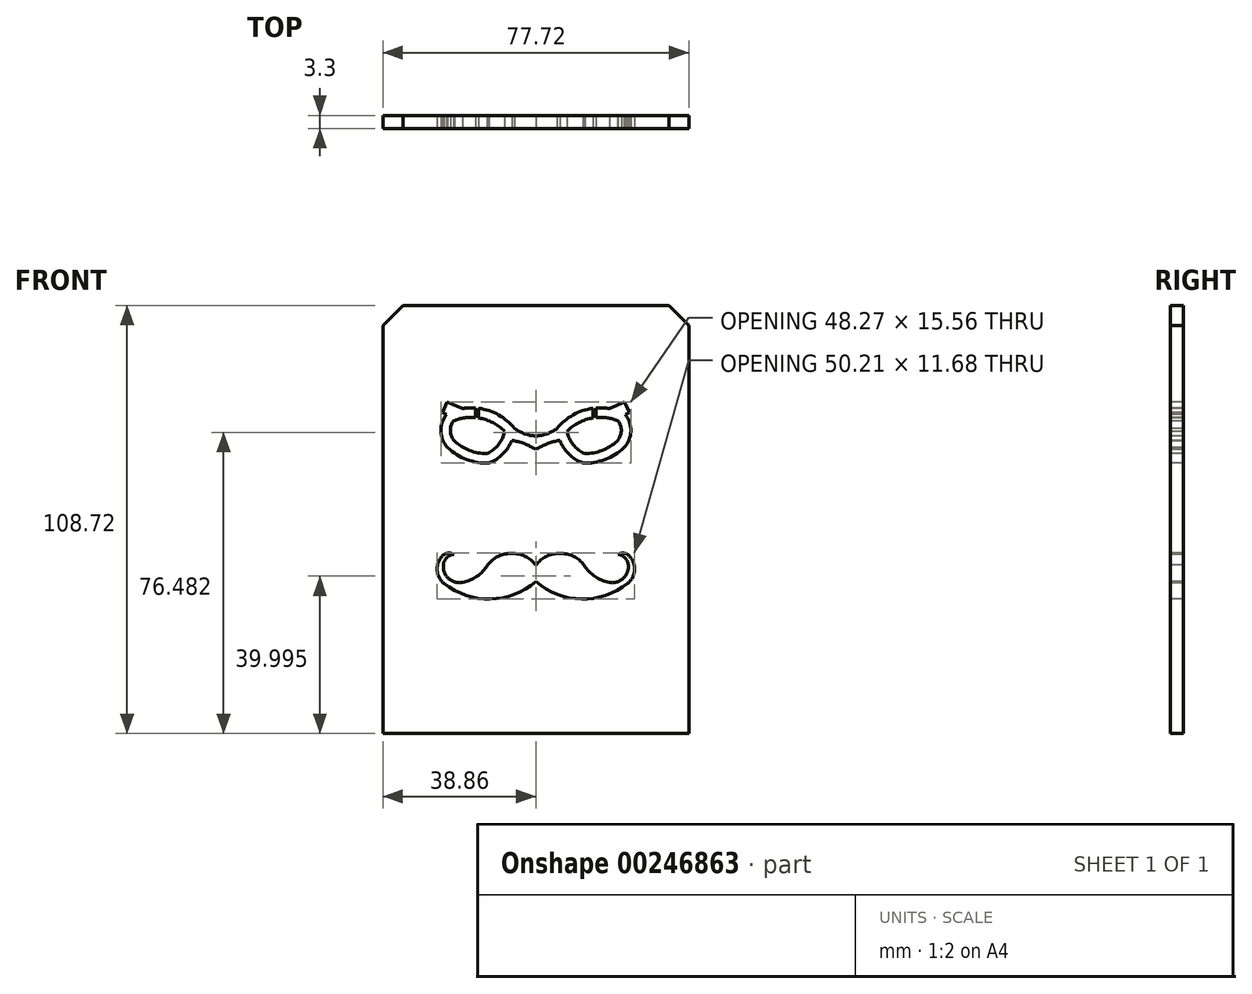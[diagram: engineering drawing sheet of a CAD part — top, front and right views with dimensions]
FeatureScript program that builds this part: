
annotation { "Feature Type Name" : "Feature", "Feature Type Description" : "" }
export const myFeature = defineFeature(function(context is Context, id is Id, definition is map)
    precondition{}
    {
        {
            var Q0;
            Q0=qCreatedBy(makeId("Front.planeOp"),FACE);
            var sketch = newSketch(context, id + "F0", { "sketchPlane" : qUnion([Q0])});
            skLineSegment(sketch, "E0.bottom", {"start": v(38.86, 54.36) * mm, "end": v(-38.86, 54.36) * mm});
            skLineSegment(sketch, "E0.top", {"start": v(38.86, -54.36) * mm, "end": v(-38.86, -54.36) * mm});
            skLineSegment(sketch, "E0.left", {"start": v(38.86, 54.36) * mm, "end": v(38.86, -54.36) * mm});
            skLineSegment(sketch, "E0.right", {"start": v(-38.86, 54.36) * mm, "end": v(-38.86, -54.36) * mm});
            skPoint(sketch, "E0.middle", {"position": v(0, 0) * mm});
            skSolve(sketch);
        }
        {
            var Q0;
            Q0=qSketchRegion(id+"F0",true);
            extrude(context, id + "F1", {"entities" : qUnion([Q0]), "depth" : 3.3 * mm});
        }
        {
            var Q0;
            Q0=makeQuery(id+"F1.opExtrude","CAP_FACE",FACE,{"disambiguationData":[OSD([sQuery(id+"F0.wireOp",EDGE,"E0.bottom"),sQuery(id+"F0.wireOp",EDGE,"E0.top"),sQuery(id+"F0.wireOp",EDGE,"E0.left"),sQuery(id+"F0.wireOp",EDGE,"E0.right")])],"isStart":false});
            var sketch = newSketch(context, id + "F2", { "sketchPlane" : qUnion([Q0])});
            skLineSegment(sketch, "E1", {"start": v(0, 57.24) * mm, "end": v(0, -57.24) * mm, "construction": true});
            skLineSegment(sketch, "E2", {"start": v(-50.8, 0) * mm, "end": v(50.8, 0) * mm, "construction": true});
            skArc(sketch, "E3", {"start": v(35.44, -3.57) * mm, "mid": v(31.46, -11.87) * mm, "end": v(32.26, -21.03) * mm});
            skLineSegment(sketch, "E4", {"start": v(15.88, -44.54) * mm, "end": v(0, -44.54) * mm, "construction": true});
            skArc(sketch, "E5", {"start": v(15.88, -44.54) * mm, "mid": v(30.2, -37.06) * mm, "end": v(32.26, -21.03) * mm});
            skArc(sketch, "E6", {"start": v(15.88, -44.54) * mm, "mid": v(7.78, -45.34) * mm, "end": v(0, -47.71) * mm});
            skArc(sketch, "E7.MirrorCS", {"start": v(-15.87, -44.54) * mm, "mid": v(-7.78, -45.34) * mm, "end": v(0, -47.71) * mm});
            skArc(sketch, "E8.MirrorCS", {"start": v(-15.87, -44.54) * mm, "mid": v(-30.2, -37.06) * mm, "end": v(-32.26, -21.03) * mm});
            skArc(sketch, "E9.MirrorCS", {"start": v(-35.44, -3.57) * mm, "mid": v(-31.46, -11.87) * mm, "end": v(-32.26, -21.03) * mm});
            skArc(sketch, "E10.MirrorCS", {"start": v(-35.44, 3.57) * mm, "mid": v(-31.46, 11.87) * mm, "end": v(-32.26, 21.03) * mm});
            skArc(sketch, "E11.MirrorCS", {"start": v(-15.88, 44.54) * mm, "mid": v(-30.2, 37.06) * mm, "end": v(-32.26, 21.03) * mm});
            skArc(sketch, "E12.MirrorCS", {"start": v(-15.88, 44.54) * mm, "mid": v(-7.78, 45.34) * mm, "end": v(0, 47.71) * mm});
            skArc(sketch, "E13.MirrorCS", {"start": v(15.87, 44.54) * mm, "mid": v(7.78, 45.34) * mm, "end": v(0, 47.71) * mm});
            skArc(sketch, "E14.MirrorCS", {"start": v(15.87, 44.54) * mm, "mid": v(30.2, 37.06) * mm, "end": v(32.26, 21.03) * mm});
            skArc(sketch, "E15.MirrorCS", {"start": v(35.44, 3.57) * mm, "mid": v(31.46, 11.87) * mm, "end": v(32.26, 21.03) * mm});
            skArc(sketch, "E16", {"start": v(35.44, 3.57) * mm, "mid": v(34.41, 0) * mm, "end": v(35.44, -3.57) * mm});
            skPoint(sketch, "E17.orphan", {"position": v(39.69, 0) * mm});
            skArc(sketch, "E18.MirrorCS", {"start": v(-35.44, 3.57) * mm, "mid": v(-34.41, 0) * mm, "end": v(-35.44, -3.57) * mm});
            skPoint(sketch, "E19.orphan", {"position": v(-39.69, 0) * mm});
            skSolve(sketch);
        }
        {
            var Q0;
            Q0=makeQuery(id+"F2.imprint","IMPRINT",FACE,{"disambiguationData":[TD([[makeQuery(id+"F2.imprint","IMPRINT",EDGE,{"derivedFrom":sQuery(id+"F2.wireOp",EDGE,"E3")}),1.0]])]});
            var sketch = newSketch(context, id + "F3", { "sketchPlane" : qUnion([Q0])});
            skFitSpline(sketch, "E20", {"points": [v(-34.74, -25) * mm, v(-17.68, -23.14) * mm, v(0, -25.84) * mm, v(18.3, -28) * mm, v(33.6, -24.4) * mm], "startDerivative": vector(68.08, 28.42) * mm, "endDerivative": vector(41.75, 55.86) * mm});
            skArc(sketch, "E21.0", {"start": v(15.88, -44.54) * mm, "mid": v(28.97, -38.63) * mm, "end": v(33.2, -24.9) * mm});
            skArc(sketch, "E22.0", {"start": v(-15.87, -44.54) * mm, "mid": v(-29.14, -38.43) * mm, "end": v(-33.13, -24.38) * mm});
            skArc(sketch, "E23.0", {"start": v(15.88, -44.54) * mm, "mid": v(7.78, -45.34) * mm, "end": v(0, -47.71) * mm});
            skArc(sketch, "E23.1", {"start": v(-15.87, -44.54) * mm, "mid": v(-7.78, -45.34) * mm, "end": v(0, -47.71) * mm});
            skPoint(sketch, "E24.orphan", {"position": v(-32.26, -21.03) * mm});
            skLineSegment(sketch, "E25.bottom", {"start": v(23.58, -32.65) * mm, "end": v(5.44, -32.65) * mm, "construction": true});
            skLineSegment(sketch, "E25.top", {"start": v(23.58, -12.55) * mm, "end": v(5.44, -12.55) * mm, "construction": true});
            skLineSegment(sketch, "E25.left", {"start": v(23.58, -32.65) * mm, "end": v(23.58, -12.55) * mm, "construction": true});
            skLineSegment(sketch, "E25.right", {"start": v(5.44, -32.65) * mm, "end": v(5.44, -12.55) * mm, "construction": true});
            skArc(sketch, "E26", {"start": v(6.5, -26.77) * mm, "mid": v(6.6, -19.6) * mm, "end": v(5.44, -12.55) * mm});
            skArc(sketch, "E27", {"start": v(23.58, -12.55) * mm, "mid": v(22.47, -20.37) * mm, "end": v(22.78, -28.26) * mm});
            skLineSegment(sketch, "E28", {"start": v(0.57, -13.45) * mm, "end": v(5.44, -12.55) * mm});
            skLineSegment(sketch, "E29", {"start": v(28.46, 0) * mm, "end": v(0.57, 0) * mm, "construction": true});
            skArc(sketch, "E30", {"start": v(-2.4, -8.48) * mm, "mid": v(-2.65, -12) * mm, "end": v(0.57, -13.45) * mm});
            skArc(sketch, "E31", {"start": v(0, -10.42) * mm, "mid": v(-0.23, -8.24) * mm, "end": v(-2.4, -8.48) * mm});
            skArc(sketch, "E32", {"start": v(0, -10.42) * mm, "mid": v(-0.04, -11.92) * mm, "end": v(1.4, -12.35) * mm});
            skArc(sketch, "E33", {"start": v(1.4, -12.35) * mm, "mid": v(5.55, -5.86) * mm, "end": v(0.57, 0) * mm});
            skLineSegment(sketch, "E34", {"start": v(14.51, 0) * mm, "end": v(14.51, -12.55) * mm, "construction": true});
            skArc(sketch, "E35.MirrorCS", {"start": v(27.61, -12.35) * mm, "mid": v(23.47, -5.86) * mm, "end": v(28.46, 0) * mm});
            skLineSegment(sketch, "E36.MirrorCS", {"start": v(28.46, -13.45) * mm, "end": v(23.58, -12.55) * mm});
            skArc(sketch, "E37.MirrorCS", {"start": v(31.42, -8.48) * mm, "mid": v(31.67, -12) * mm, "end": v(28.46, -13.45) * mm});
            skArc(sketch, "E38.MirrorCS", {"start": v(29.02, -10.42) * mm, "mid": v(29.25, -8.24) * mm, "end": v(31.42, -8.48) * mm});
            skArc(sketch, "E39.MirrorCS", {"start": v(29.02, -10.42) * mm, "mid": v(29.06, -11.92) * mm, "end": v(27.61, -12.35) * mm});
            skArc(sketch, "E40", {"start": v(0.57, 0) * mm, "mid": v(5.65, -0.6) * mm, "end": v(10.76, -0.93) * mm});
            skLineSegment(sketch, "E41", {"start": v(10.76, -0.93) * mm, "end": v(8.47, 9.06) * mm});
            skLineSegment(sketch, "E42", {"start": v(8.47, 9.06) * mm, "end": v(6.8, 8.68) * mm});
            skArc(sketch, "E43", {"start": v(7.7, 9.94) * mm, "mid": v(5.6, 10.49) * mm, "end": v(6.8, 8.68) * mm});
            skLineSegment(sketch, "E44", {"start": v(14.51, 0) * mm, "end": v(14.77, 8.31) * mm, "construction": true});
            skLineSegment(sketch, "E45.MirrorCS", {"start": v(18.26, -0.93) * mm, "end": v(21.1, 8.66) * mm});
            skLineSegment(sketch, "E46.MirrorCS", {"start": v(21.1, 8.66) * mm, "end": v(22.75, 8.18) * mm});
            skArc(sketch, "E47.MirrorCS", {"start": v(21.93, 9.5) * mm, "mid": v(24.07, 9.9) * mm, "end": v(22.75, 8.18) * mm});
            skArc(sketch, "E48", {"start": v(7.7, 9.94) * mm, "mid": v(12.62, 15.22) * mm, "end": v(14.1, 22.28) * mm});
            skArc(sketch, "E49", {"start": v(15.59, 22.28) * mm, "mid": v(17.1, 15.06) * mm, "end": v(21.93, 9.5) * mm});
            skLineSegment(sketch, "E50", {"start": v(14.1, 22.28) * mm, "end": v(12.75, 29.94) * mm});
            skLineSegment(sketch, "E51", {"start": v(12.75, 29.94) * mm, "end": v(10.25, 29.5) * mm});
            skLineSegment(sketch, "E52", {"start": v(10.25, 29.5) * mm, "end": v(10.04, 30.72) * mm});
            skLineSegment(sketch, "E53", {"start": v(10.04, 30.72) * mm, "end": v(12.66, 31.3) * mm});
            skLineSegment(sketch, "E54", {"start": v(12.66, 31.3) * mm, "end": v(12.12, 34.79) * mm});
            skLineSegment(sketch, "E55", {"start": v(12.12, 34.79) * mm, "end": v(14.24, 35.11) * mm});
            skLineSegment(sketch, "E56", {"start": v(14.24, 35.11) * mm, "end": v(14.8, 31.45) * mm});
            skLineSegment(sketch, "E57", {"start": v(14.8, 31.45) * mm, "end": v(17.72, 31.9) * mm});
            skLineSegment(sketch, "E58", {"start": v(17.72, 31.9) * mm, "end": v(17.99, 30.17) * mm});
            skLineSegment(sketch, "E59", {"start": v(17.99, 30.17) * mm, "end": v(14.89, 29.68) * mm});
            skLineSegment(sketch, "E60", {"start": v(14.89, 29.68) * mm, "end": v(15.59, 22.28) * mm});
            skArc(sketch, "E61.trimOffspring", {"start": v(18.26, -0.93) * mm, "mid": v(23.37, -0.6) * mm, "end": v(28.46, 0) * mm});
            skPoint(sketch, "E62.orphan", {"position": v(18.2, -1.17) * mm});
            skLineSegment(sketch, "E63", {"start": v(8.48, -4.98) * mm, "end": v(9.12, -7.41) * mm});
            skLineSegment(sketch, "E64", {"start": v(9.77, -9.85) * mm, "end": v(10.94, -9.54) * mm});
            skLineSegment(sketch, "E65", {"start": v(12.72, -9.06) * mm, "end": v(12.26, -7.34) * mm});
            skLineSegment(sketch, "E66", {"start": v(11.56, -4.7) * mm, "end": v(10.33, -4.82) * mm});
            skLineSegment(sketch, "E67", {"start": v(9.75, -4.87) * mm, "end": v(10.34, -7.13) * mm});
            skLineSegment(sketch, "E68", {"start": v(10.34, -7.13) * mm, "end": v(9.12, -7.41) * mm});
            skLineSegment(sketch, "E69", {"start": v(10.33, -4.82) * mm, "end": v(10.9, -7.06) * mm});
            skLineSegment(sketch, "E70", {"start": v(10.9, -7.06) * mm, "end": v(12.14, -6.89) * mm});
            skLineSegment(sketch, "E71", {"start": v(9.29, -8.05) * mm, "end": v(10.46, -7.73) * mm});
            skLineSegment(sketch, "E72", {"start": v(10.46, -7.73) * mm, "end": v(10.94, -9.54) * mm});
            skLineSegment(sketch, "E73", {"start": v(11.57, -9.37) * mm, "end": v(11.12, -7.64) * mm});
            skLineSegment(sketch, "E74", {"start": v(11.12, -7.64) * mm, "end": v(12.26, -7.34) * mm});
            skLineSegment(sketch, "E75.trimOffspring", {"start": v(12.14, -6.89) * mm, "end": v(11.56, -4.7) * mm});
            skLineSegment(sketch, "E76.trimOffspring", {"start": v(9.75, -4.87) * mm, "end": v(8.48, -4.98) * mm});
            skLineSegment(sketch, "E77.trimOffspring", {"start": v(9.29, -8.05) * mm, "end": v(9.77, -9.85) * mm});
            skLineSegment(sketch, "E78.trimOffspring", {"start": v(11.57, -9.37) * mm, "end": v(12.72, -9.06) * mm});
            skLineSegment(sketch, "E79.MirrorCS", {"start": v(17.46, -4.7) * mm, "end": v(18.69, -4.82) * mm});
            skLineSegment(sketch, "E80.MirrorCS", {"start": v(19.27, -4.87) * mm, "end": v(18.68, -7.13) * mm});
            skLineSegment(sketch, "E81.MirrorCS", {"start": v(17.45, -9.37) * mm, "end": v(17.9, -7.64) * mm});
            skLineSegment(sketch, "E82.MirrorCS", {"start": v(18.68, -7.13) * mm, "end": v(19.9, -7.41) * mm});
            skLineSegment(sketch, "E83.MirrorCS", {"start": v(17.9, -7.64) * mm, "end": v(16.76, -7.34) * mm});
            skLineSegment(sketch, "E84.MirrorCS", {"start": v(18.69, -4.82) * mm, "end": v(18.12, -7.06) * mm});
            skLineSegment(sketch, "E85.MirrorCS", {"start": v(16.88, -6.89) * mm, "end": v(17.46, -4.7) * mm});
            skLineSegment(sketch, "E86.MirrorCS", {"start": v(18.12, -7.06) * mm, "end": v(16.88, -6.89) * mm});
            skLineSegment(sketch, "E87.MirrorCS", {"start": v(19.27, -4.87) * mm, "end": v(20.54, -4.98) * mm});
            skLineSegment(sketch, "E88.MirrorCS", {"start": v(20.54, -4.98) * mm, "end": v(19.9, -7.41) * mm});
            skLineSegment(sketch, "E89.MirrorCS", {"start": v(19.73, -8.05) * mm, "end": v(18.56, -7.73) * mm});
            skLineSegment(sketch, "E90.MirrorCS", {"start": v(19.73, -8.05) * mm, "end": v(19.25, -9.85) * mm});
            skLineSegment(sketch, "E91.MirrorCS", {"start": v(19.25, -9.85) * mm, "end": v(18.08, -9.54) * mm});
            skLineSegment(sketch, "E92.MirrorCS", {"start": v(18.56, -7.73) * mm, "end": v(18.08, -9.54) * mm});
            skLineSegment(sketch, "E93.MirrorCS", {"start": v(17.45, -9.37) * mm, "end": v(16.3, -9.06) * mm});
            skLineSegment(sketch, "E94.MirrorCS", {"start": v(16.3, -9.06) * mm, "end": v(16.76, -7.34) * mm});
            skArc(sketch, "E95", {"start": v(14.28, 11.97) * mm, "mid": v(12.23, 10.98) * mm, "end": v(11.15, 8.98) * mm});
            skLineSegment(sketch, "E96", {"start": v(14.28, 11.97) * mm, "end": v(14.28, 8.98) * mm});
            skLineSegment(sketch, "E97", {"start": v(15.17, 4.65) * mm, "end": v(15.17, 7.88) * mm});
            skLineSegment(sketch, "E98", {"start": v(18.4, 8.98) * mm, "end": v(15.17, 8.98) * mm});
            skLineSegment(sketch, "E99", {"start": v(11.1, 7.88) * mm, "end": v(14.28, 7.88) * mm});
            skLineSegment(sketch, "E100.trimOffspring", {"start": v(15.17, 8.98) * mm, "end": v(15.17, 11.98) * mm});
            skLineSegment(sketch, "E101.trimOffspring", {"start": v(15.17, 7.88) * mm, "end": v(18.43, 7.88) * mm});
            skLineSegment(sketch, "E102.trimOffspring", {"start": v(14.28, 7.88) * mm, "end": v(14.28, 4.66) * mm});
            skLineSegment(sketch, "E103.trimOffspring", {"start": v(14.28, 8.98) * mm, "end": v(11.15, 8.98) * mm});
            skArc(sketch, "E104.trimOffspring", {"start": v(11.1, 7.88) * mm, "mid": v(12.14, 5.73) * mm, "end": v(14.28, 4.66) * mm});
            skArc(sketch, "E105.trimOffspring", {"start": v(18.4, 8.98) * mm, "mid": v(17.28, 11.01) * mm, "end": v(15.17, 11.98) * mm});
            skArc(sketch, "E106.trimOffspring", {"start": v(15.17, 4.65) * mm, "mid": v(17.37, 5.7) * mm, "end": v(18.43, 7.88) * mm});
            skLineSegment(sketch, "E107.left", {"start": v(12.04, -27.4) * mm, "end": v(12.04, -21.48) * mm});
            skLineSegment(sketch, "E107.right", {"start": v(16, -27.8) * mm, "end": v(16, -21.48) * mm});
            skArc(sketch, "E108", {"start": v(16, -21.48) * mm, "mid": v(14.02, -19.5) * mm, "end": v(12.04, -21.48) * mm});
            skLineSegment(sketch, "E109", {"start": v(12.04, -27.4) * mm, "end": v(16, -27.8) * mm});
            skArc(sketch, "E110.0", {"start": v(-35.44, -3.57) * mm, "mid": v(-31.46, -11.87) * mm, "end": v(-32.26, -21.03) * mm, "construction": true});
            skArc(sketch, "E110.1", {"start": v(15.87, 44.54) * mm, "mid": v(7.78, 45.34) * mm, "end": v(0, 47.71) * mm});
            skArc(sketch, "E110.2", {"start": v(-15.88, 44.54) * mm, "mid": v(-30.2, 37.06) * mm, "end": v(-32.26, 21.03) * mm, "construction": true});
            skArc(sketch, "E110.3", {"start": v(-35.44, 3.57) * mm, "mid": v(-34.41, 0) * mm, "end": v(-35.44, -3.57) * mm, "construction": true});
            skArc(sketch, "E110.4", {"start": v(-35.44, 3.57) * mm, "mid": v(-31.46, 11.87) * mm, "end": v(-32.26, 21.03) * mm});
            skArc(sketch, "E110.5", {"start": v(-15.88, 44.54) * mm, "mid": v(-7.78, 45.34) * mm, "end": v(0, 47.71) * mm});
            skArc(sketch, "E111", {"start": v(-17.1, 9.66) * mm, "mid": v(-3.37, 14.89) * mm, "end": v(1.5, 28.74) * mm});
            skArc(sketch, "E112", {"start": v(-17.1, 9.66) * mm, "mid": v(-26.87, 8.42) * mm, "end": v(-35.44, 3.57) * mm});
            skArc(sketch, "E113", {"start": v(15.87, 44.54) * mm, "mid": v(5.2, 39.82) * mm, "end": v(1.5, 28.74) * mm});
            skArc(sketch, "E114.trimOffspring", {"start": v(-15.88, 44.54) * mm, "mid": v(-30.2, 37.06) * mm, "end": v(-32.26, 21.03) * mm});
            skArc(sketch, "E115", {"start": v(-24.92, -22.89) * mm, "mid": v(-23.55, -16.2) * mm, "end": v(-24.4, -9.44) * mm});
            skFitSpline(sketch, "E116", {"points": [v(-24.4, -9.44) * mm, v(-26.98, -10.38) * mm, v(-27.97, -8.39) * mm, v(-29.93, -8.52) * mm, v(-30.92, -6) * mm, v(-32.1, -5.52) * mm, v(-32.53, -4.18) * mm, v(-32.18, -3.27) * mm, v(-31.84, -4.44) * mm, v(-31.05, -4.83) * mm, v(-31.49, -2) * mm, v(-30.88, -2.14) * mm, v(-30.1, -5.05) * mm, v(-29.45, -3.57) * mm, v(-28.71, -3.66) * mm, v(-29.54, -5.78) * mm, v(-29.23, -7.17) * mm, v(-27.54, -7.04) * mm, v(-26.28, -8.52) * mm, v(-24.4, -7.6) * mm], "startDerivative": vector(-46.53, -30.94) * mm, "endDerivative": vector(36.03, 29.74) * mm});
            skArc(sketch, "E117", {"start": v(-24.4, -7.6) * mm, "mid": v(-24.93, -4.98) * mm, "end": v(-25.9, -2.49) * mm});
            skFitSpline(sketch, "E118", {"points": [v(-25.9, -2.49) * mm, v(-27.5, -1.49) * mm, v(-28.76, -1.49) * mm, v(-29.23, 0) * mm, v(-31.14, 0) * mm, v(-30.8, 3.42) * mm, v(-29.97, 3.55) * mm, v(-30.27, 1.77) * mm, v(-29.54, 1.72) * mm, v(-28.8, 4.59) * mm, v(-27.67, 4.37) * mm, v(-28.28, 1.98) * mm, v(-27.84, 0) * mm, v(-27.2, 2.46) * mm, v(-25.9, 2.37) * mm, v(-25.9, 0) * mm, v(-24.11, -2.49) * mm, v(-22.72, -5.26) * mm, v(-21.68, -4.18) * mm, v(-23.16, 1.33) * mm, v(-20.82, 1.46) * mm, v(-20.82, 3.02) * mm], "startDerivative": vector(-33.14, 31.82) * mm, "endDerivative": vector(-15.18, 49.9) * mm});
            skFitSpline(sketch, "E119", {"points": [v(-20.82, 3.02) * mm, v(-19.2, 3.92) * mm, v(-20.04, 5.84) * mm, v(-20.82, 8.3) * mm, v(-20.04, 8.38) * mm, v(-19.62, 6.46) * mm, v(-18.62, 5.34) * mm, v(-18.96, 7.3) * mm, v(-18.2, 7.55) * mm, v(-18.12, 4.13) * mm, v(-19.33, 2.25) * mm, v(-19.46, 0.87) * mm, v(-20.82, 0) * mm, v(-20.04, -3.35) * mm, v(-16.32, 0) * mm, v(-17.1, 1.46) * mm, v(-15.74, 3.02) * mm, v(-15.45, 5.84) * mm, v(-14.49, 5.55) * mm, v(-14.82, 3.02) * mm, v(-14.53, 1.46) * mm, v(-13.36, 4) * mm, v(-12.02, 3.02) * mm, v(-14.2, 0) * mm, v(-17.1, -4.06) * mm, v(-17.1, -7.4) * mm, v(-14.36, -5.44) * mm, v(-14.57, -4.1) * mm, v(-12.78, -3.22) * mm, v(-12.53, -1.68) * mm, v(-10.44, -0.8) * mm, v(-10.27, 1.46) * mm, v(-9.35, 0) * mm, v(-8.6, 3.02) * mm, v(-8.1, 0) * mm, v(-9.44, -1.26) * mm, v(-11.31, -3.26) * mm, v(-13.15, -4.6) * mm, v(-13.36, -6.6) * mm, v(-15.78, -8.94) * mm], "startDerivative": vector(94.65, 30.69) * mm, "endDerivative": vector(-102.82, -69.25) * mm});
            skArc(sketch, "E120", {"start": v(-15.78, -8.94) * mm, "mid": v(-16.8, -16.14) * mm, "end": v(-15.78, -23.34) * mm});
            skFitSpline(sketch, "E121", {"points": [v(-22.4, -11.55) * mm, v(-21.43, -13.07) * mm, v(-21.4, -14.11) * mm, v(-20.72, -14.36) * mm, v(-20.54, -13.59) * mm, v(-20.94, -12.02) * mm, v(-21.71, -11.06) * mm, v(-22.67, -10.07) * mm, v(-22.4, -11.55) * mm]});
            skFitSpline(sketch, "E122", {"points": [v(-18.38, -10.1) * mm, v(-19.09, -11.5) * mm, v(-19.21, -12.7) * mm, v(-19.15, -14.02) * mm, v(-18.84, -14.6) * mm, v(-18.38, -14.05) * mm, v(-18.26, -13.1) * mm, v(-18.56, -12.32) * mm, v(-18.29, -11.28) * mm, v(-17.6, -10.38) * mm, v(-18.38, -10.1) * mm]});
            skFitSpline(sketch, "E123", {"points": [v(-20.3, -15.78) * mm, v(-20.35, -17.1) * mm, v(-20.9, -18.47) * mm, v(-21.8, -19.67) * mm, v(-21.9, -21.46) * mm, v(-20.45, -21.43) * mm, v(-19.64, -20.38) * mm, v(-19.43, -18.84) * mm, v(-19.7, -17.85) * mm, v(-19.7, -16.37) * mm, v(-19.43, -15.38) * mm, v(-20.3, -15.78) * mm]});
            skCircle(sketch, "E124", {"center": v(-15.88, 27.08) * mm, "radius": 13.34 * mm});
            skSolve(sketch);
        }
        {
            var Q0;
            Q0=qSketchRegion(id+"F3",true);
            extrude(context, id + "F4", {"entities" : qUnion([Q0]), "operationType" : NewBodyOperationType.ADD, "oppositeDirection" : true, "depth" : 3.3 * mm});
        }
        {
            var Q0;
            Q0=makeQuery(id+"F1.opExtrude","SWEPT_EDGE",EDGE,{"disambiguationData":[OSD([sQuery(id+"F0.wireOp",EDGE,"E0.bottom"),sQuery(id+"F0.wireOp",EDGE,"E0.right")])]});
            var Q1;
            Q1=makeQuery(id+"F1.opExtrude","SWEPT_EDGE",EDGE,{"disambiguationData":[OSD([sQuery(id+"F0.wireOp",EDGE,"E0.bottom"),sQuery(id+"F0.wireOp",EDGE,"E0.left")])]});
            chamfer(context, id + "F5", {"entities" : qUnion([Q0, Q1]), "width" : 5.08 * mm, "tangentPropagation" : true});
        }
        {
            var Q0;
            Q0=makeQuery(id+"F2.imprint","IMPRINT",FACE,{"disambiguationData":[TD([[makeQuery(id+"F2.imprint","IMPRINT",EDGE,{"derivedFrom":sQuery(id+"F2.wireOp",EDGE,"E3")}),-1.0]])]});
            var sketch = newSketch(context, id + "F6", { "sketchPlane" : qUnion([Q0])});
            skArc(sketch, "E125", {"start": v(6.08, 20.1) * mm, "mid": v(8.4, 16.62) * mm, "end": v(11.92, 14.34) * mm});
            skArc(sketch, "E126", {"start": v(11.92, 14.34) * mm, "mid": v(17.55, 15.25) * mm, "end": v(22.4, 18.27) * mm});
            skArc(sketch, "E127", {"start": v(22.4, 18.27) * mm, "mid": v(24.13, 22.42) * mm, "end": v(22.71, 26.69) * mm});
            skArc(sketch, "E128", {"start": v(18.65, 28.2) * mm, "mid": v(16.98, 28.36) * mm, "end": v(15.3, 28.33) * mm});
            skArc(sketch, "E129.0", {"start": v(20.92, 25.07) * mm, "mid": v(18.16, 25.83) * mm, "end": v(15.3, 25.9) * mm});
            skArc(sketch, "E129.1", {"start": v(20.68, 19.97) * mm, "mid": v(21.72, 22.48) * mm, "end": v(20.92, 25.07) * mm});
            skArc(sketch, "E129.2", {"start": v(12.43, 16.74) * mm, "mid": v(16.86, 17.57) * mm, "end": v(20.68, 19.97) * mm});
            skArc(sketch, "E129.3", {"start": v(7.92, 22.36) * mm, "mid": v(9.5, 19) * mm, "end": v(12.43, 16.74) * mm});
            skArc(sketch, "E130", {"start": v(0, 21.24) * mm, "mid": v(2.83, 21.78) * mm, "end": v(5.38, 23.13) * mm});
            skArc(sketch, "E131", {"start": v(6.08, 20.1) * mm, "mid": v(2.93, 19.26) * mm, "end": v(0, 17.8) * mm});
            skLineSegment(sketch, "E132", {"start": v(18.65, 28.2) * mm, "end": v(22.54, 29.9) * mm});
            skLineSegment(sketch, "E133", {"start": v(22.54, 29.9) * mm, "end": v(23.75, 27.14) * mm});
            skLineSegment(sketch, "E134", {"start": v(23.75, 27.14) * mm, "end": v(22.71, 26.69) * mm});
            skPoint(sketch, "E135.orphan", {"position": v(22.4, 27.06) * mm});
            skArc(sketch, "E136", {"start": v(0, -15.75) * mm, "mid": v(11.58, -20.2) * mm, "end": v(23.33, -16.24) * mm});
            skArc(sketch, "E137", {"start": v(23.33, -16.24) * mm, "mid": v(25.1, -12.56) * mm, "end": v(23.33, -8.89) * mm});
            skArc(sketch, "E138", {"start": v(23.33, -8.89) * mm, "mid": v(22.07, -8.52) * mm, "end": v(20.8, -8.89) * mm});
            skArc(sketch, "E139", {"start": v(23.33, -10.83) * mm, "mid": v(22.38, -9.45) * mm, "end": v(20.8, -8.89) * mm});
            skArc(sketch, "E140", {"start": v(18.65, -15.99) * mm, "mid": v(22.45, -14.73) * mm, "end": v(23.33, -10.83) * mm});
            skArc(sketch, "E141", {"start": v(12.27, -11.6) * mm, "mid": v(15, -14.45) * mm, "end": v(18.65, -15.99) * mm});
            skArc(sketch, "E142", {"start": v(12.27, -11.6) * mm, "mid": v(6.14, -8.58) * mm, "end": v(0, -11.6) * mm});
            skArc(sketch, "E143.MirrorCS", {"start": v(-12.27, -11.6) * mm, "mid": v(-6.14, -8.58) * mm, "end": v(0, -11.6) * mm});
            skArc(sketch, "E144.MirrorCS", {"start": v(-12.27, -11.6) * mm, "mid": v(-15, -14.45) * mm, "end": v(-18.65, -15.99) * mm});
            skArc(sketch, "E145.MirrorCS", {"start": v(0, -15.75) * mm, "mid": v(-11.58, -20.2) * mm, "end": v(-23.33, -16.24) * mm});
            skArc(sketch, "E146.MirrorCS", {"start": v(-23.33, -16.24) * mm, "mid": v(-25.1, -12.56) * mm, "end": v(-23.33, -8.89) * mm});
            skArc(sketch, "E147.MirrorCS", {"start": v(-23.33, -8.89) * mm, "mid": v(-22.07, -8.52) * mm, "end": v(-20.8, -8.89) * mm});
            skArc(sketch, "E148.MirrorCS", {"start": v(-23.33, -10.83) * mm, "mid": v(-22.38, -9.45) * mm, "end": v(-20.8, -8.89) * mm});
            skArc(sketch, "E149.MirrorCS", {"start": v(-18.65, -15.99) * mm, "mid": v(-22.45, -14.73) * mm, "end": v(-23.33, -10.83) * mm});
            skArc(sketch, "E150.MirrorCS", {"start": v(0, 21.24) * mm, "mid": v(-2.83, 21.78) * mm, "end": v(-5.38, 23.13) * mm});
            skArc(sketch, "E151.MirrorCS", {"start": v(-6.08, 20.1) * mm, "mid": v(-2.93, 19.26) * mm, "end": v(0, 17.8) * mm});
            skArc(sketch, "E152.MirrorCS", {"start": v(-6.08, 20.1) * mm, "mid": v(-8.4, 16.62) * mm, "end": v(-11.92, 14.34) * mm});
            skArc(sketch, "E153.MirrorCS", {"start": v(-11.92, 14.34) * mm, "mid": v(-17.55, 15.25) * mm, "end": v(-22.4, 18.27) * mm});
            skArc(sketch, "E154.MirrorCS", {"start": v(-12.43, 16.74) * mm, "mid": v(-16.86, 17.57) * mm, "end": v(-20.68, 19.97) * mm});
            skArc(sketch, "E155.MirrorCS", {"start": v(-22.4, 18.27) * mm, "mid": v(-24.13, 22.42) * mm, "end": v(-22.71, 26.69) * mm});
            skLineSegment(sketch, "E156.MirrorCS", {"start": v(-23.75, 27.14) * mm, "end": v(-22.71, 26.69) * mm});
            skLineSegment(sketch, "E157.MirrorCS", {"start": v(-22.54, 29.9) * mm, "end": v(-23.75, 27.14) * mm});
            skLineSegment(sketch, "E158.MirrorCS", {"start": v(-18.65, 28.2) * mm, "end": v(-22.54, 29.9) * mm});
            skArc(sketch, "E159.MirrorCS", {"start": v(-18.65, 28.2) * mm, "mid": v(-16.98, 28.36) * mm, "end": v(-15.3, 28.33) * mm});
            skArc(sketch, "E160.MirrorCS", {"start": v(-7.92, 22.36) * mm, "mid": v(-9.5, 19) * mm, "end": v(-12.43, 16.74) * mm});
            skArc(sketch, "E161.MirrorCS", {"start": v(-20.68, 19.97) * mm, "mid": v(-21.72, 22.48) * mm, "end": v(-20.92, 25.07) * mm});
            skArc(sketch, "E162.MirrorCS", {"start": v(-20.92, 25.07) * mm, "mid": v(-18.16, 25.83) * mm, "end": v(-15.3, 25.9) * mm});
            skLineSegment(sketch, "E163.left", {"start": v(-15.3, 28.33) * mm, "end": v(-15.3, 25.9) * mm});
            skLineSegment(sketch, "E163.right", {"start": v(-14.51, 28.24) * mm, "end": v(-14.51, 25.8) * mm});
            skArc(sketch, "E164.trimOffspring", {"start": v(-14.51, 28.24) * mm, "mid": v(-9.46, 26.56) * mm, "end": v(-5.38, 23.13) * mm});
            skArc(sketch, "E165.trimOffspring", {"start": v(-14.51, 25.8) * mm, "mid": v(-10.94, 24.61) * mm, "end": v(-7.92, 22.36) * mm});
            skLineSegment(sketch, "E166.MirrorCS", {"start": v(14.51, 28.24) * mm, "end": v(14.51, 25.8) * mm});
            skLineSegment(sketch, "E167.MirrorCS", {"start": v(15.3, 28.33) * mm, "end": v(15.3, 25.9) * mm});
            skArc(sketch, "E168.trimOffspring", {"start": v(14.51, 28.24) * mm, "mid": v(9.46, 26.56) * mm, "end": v(5.38, 23.13) * mm});
            skArc(sketch, "E169.trimOffspring", {"start": v(14.51, 25.8) * mm, "mid": v(10.94, 24.61) * mm, "end": v(7.92, 22.36) * mm});
            skSolve(sketch);
        }
        {
            var Q0;
            Q0 = qSketchRegion(id + "F6", true);
            extrude(context, id + "F7", {"entities" : qUnion([Q0]), "operationType" : NewBodyOperationType.REMOVE, "endBound" : BoundingType.THROUGH_ALL, "oppositeDirection" : true, "depth" : 25.4 * mm});
        }
    });
